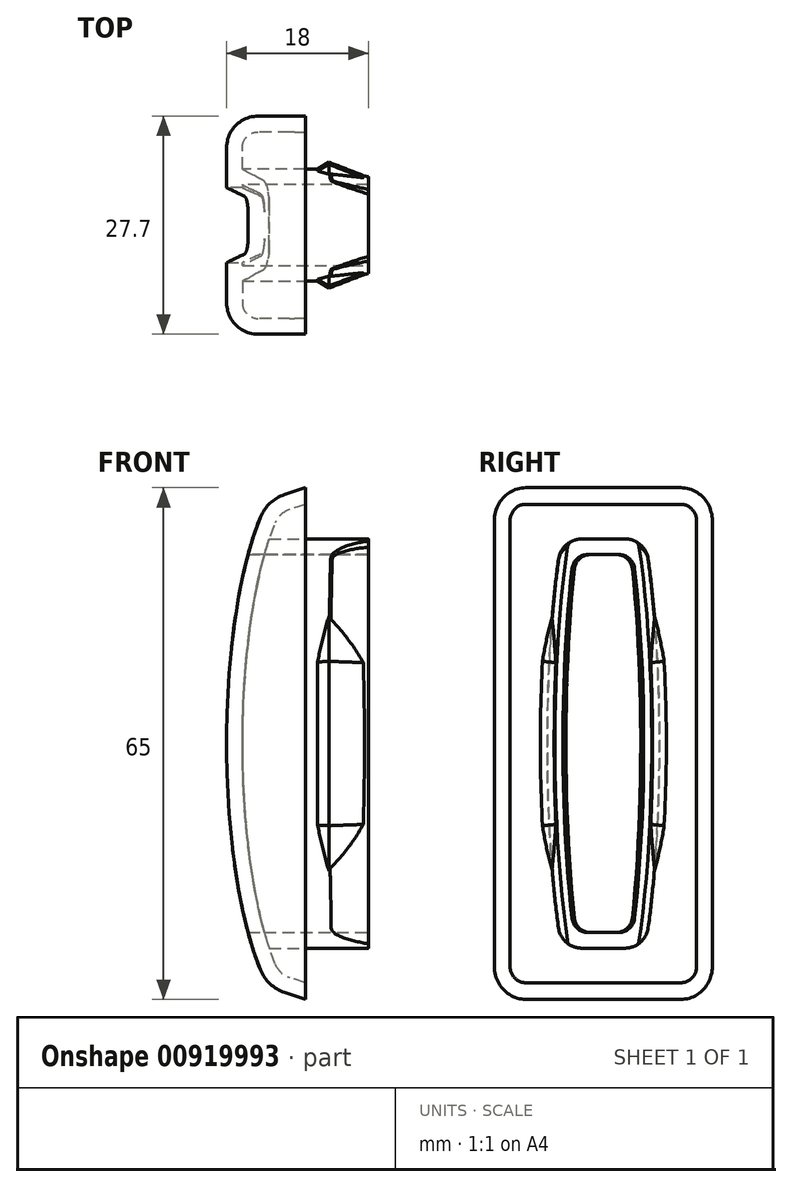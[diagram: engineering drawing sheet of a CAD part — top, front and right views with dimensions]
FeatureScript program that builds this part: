
annotation { "Feature Type Name" : "Feature", "Feature Type Description" : "" }
export const myFeature = defineFeature(function(context is Context, id is Id, definition is map)
    precondition{}
    {
        {
            var Q0;
            Q0=qCreatedBy(makeId("Front.planeOp"),FACE);
            var sketch = newSketch(context, id + "F0", { "sketchPlane" : qUnion([Q0])});
            skLineSegment(sketch, "E0", {"start": v(0, 32.5) * mm, "end": v(0, -32.5) * mm});
            skPoint(sketch, "E1", {"position": v(-10, 0) * mm});
            skPoint(sketch, "E2", {"position": v(0, 35) * mm});
            skEllipse(sketch, "E3", {"center": v(0, 0) * mm, "majorRadius": 35 * mm, "minorRadius": 10 * mm, "majorAxis": v(0, 1)});
            skPoint(sketch, "E4", {"position": v(-3, 31.5) * mm});
            skPoint(sketch, "E5", {"position": v(-3, -31.5) * mm});
            skLineSegment(sketch, "E6", {"start": v(0, -32.5) * mm, "end": v(-3, -31.5) * mm});
            skLineSegment(sketch, "E7", {"start": v(-3, -31.5) * mm, "end": v(-4.67, -30.94) * mm});
            skLineSegment(sketch, "E8", {"start": v(0, 32.5) * mm, "end": v(-3, 31.5) * mm});
            skLineSegment(sketch, "E9", {"start": v(-3, 31.5) * mm, "end": v(-4.67, 30.94) * mm});
            skSolve(sketch);
        }
        {
            var Q0;
            Q0=makeQuery(id+"F0.imprint","IMPRINT",FACE,{"disambiguationData":[TD([[makeQuery(id+"F0.imprint","IMPRINT",EDGE,{"derivedFrom":sQuery(id+"F0.wireOp",EDGE,"E0")}),-1.0]])]});
            extrude(context, id + "F1", {"entities" : qUnion([Q0]), "depth" : 13.85 * mm, "offsetDistance" : 25 * mm, "hasSecondDirection" : true, "secondDirectionOppositeDirection" : true, "secondDirectionDepth" : 13.85 * mm});
        }
        {
            var Q0;
            Q0=makeQuery(id+"F1.opExtrude","SWEPT_EDGE",EDGE,{"disambiguationData":[OSD([sQuery(id+"F0.wireOp",EDGE,"E3"),sQuery(id+"F0.wireOp",EDGE,"E7")])]});
            var Q1;
            Q1=makeQuery(id+"F1.opExtrude","SWEPT_EDGE",EDGE,{"disambiguationData":[OSD([sQuery(id+"F0.wireOp",EDGE,"E3"),sQuery(id+"F0.wireOp",EDGE,"E9")])]});
            fillet(context, id + "F2", {"entities" : qUnion([Q0, Q1]), "radius" : 5 * mm, "tangentPropagation" : true, "allowEdgeOverflow" : false});
        }
        {
            var Q0;
            Q0=makeQuery(id+"F1.opExtrude","CAP_EDGE",EDGE,{"disambiguationData":[OSD([sQuery(id+"F0.wireOp",EDGE,"E3")])],"isStart":false});
            var Q1;
            Q1=makeQuery(id+"F1.opExtrude","CAP_EDGE",EDGE,{"disambiguationData":[OSD([sQuery(id+"F0.wireOp",EDGE,"E3")])],"isStart":true});
            fillet(context, id + "F3", {"entities" : qUnion([Q0, Q1]), "radius" : 4 * mm, "tangentPropagation" : true, "allowEdgeOverflow" : false});
        }
        {
            var Q0;
            Q0=makeQuery(id+"F1.opExtrude","SWEPT_FACE",FACE,{"disambiguationData":[OSD([sQuery(id+"F0.wireOp",EDGE,"E0")])]});
            shell(context, id + "F4", {"entities" : qUnion([Q0]), "thickness" : 2 * mm});
        }
        {
            var Q0;
            Q0=qCreatedBy(makeId("Right.planeOp"),FACE);
            var sketch = newSketch(context, id + "F5", { "sketchPlane" : qUnion([Q0])});
            skPoint(sketch, "E10", {"position": v(0, 24) * mm});
            skPoint(sketch, "E11", {"position": v(5.12, 0) * mm});
            skPoint(sketch, "E12", {"position": v(3.5, 24.03) * mm});
            skPoint(sketch, "E13", {"position": v(0, 35) * mm});
            skEllipse(sketch, "E14", {"center": v(0, 0) * mm, "majorRadius": 5.12 * mm, "minorRadius": 35 * mm, "majorAxis": v(1, 0)});
            skLineSegment(sketch, "E15", {"start": v(0, 24) * mm, "end": v(7.2, 24.03) * mm});
            skLineSegment(sketch, "E16", {"start": v(0, -24) * mm, "end": v(3.73, -24) * mm});
            skLineSegment(sketch, "E17", {"start": v(0, -24) * mm, "end": v(-3.73, -24) * mm});
            skPoint(sketch, "E18", {"position": v(-4.75, 0) * mm});
            skEllipse(sketch, "E19", {"center": v(0, 0) * mm, "majorRadius": 4.75 * mm, "minorRadius": 35 * mm, "majorAxis": v(-1, 0)});
            skLineSegment(sketch, "E20", {"start": v(0, 24) * mm, "end": v(-5.9, 24) * mm});
            skLineSegment(sketch, "E21", {"start": v(-5.36, 25.98) * mm, "end": v(6.58, 26.03) * mm});
            skLineSegment(sketch, "E22", {"start": v(-8.21, -26) * mm, "end": v(8.3, -26) * mm});
            skPoint(sketch, "E23", {"position": v(7.12, 0) * mm});
            skPoint(sketch, "E24", {"position": v(0, 39) * mm});
            skEllipse(sketch, "E25", {"center": v(0, 0) * mm, "majorRadius": 7.12 * mm, "minorRadius": 39 * mm, "majorAxis": v(1, 0)});
            skPoint(sketch, "E26", {"position": v(6.12, 0) * mm});
            skPoint(sketch, "E27", {"position": v(0, 37) * mm});
            skEllipse(sketch, "E28", {"center": v(0, 0) * mm, "majorRadius": 6.12 * mm, "minorRadius": 37 * mm, "majorAxis": v(1, 0)});
            skSolve(sketch);
        }
        {
            var Q0;
            {var subQ5=sQuery(id+"F5.wireOp",EDGE,"E15");var subQ8=sQuery(id+"F5.wireOp",EDGE,"E20");var subQ9=makeQuery(id+"F5.imprint","INTERSECT",VERTEX,{"derivedFrom":[subQ5,subQ8]});Q0=makeQuery(id+"F5.imprint","IMPRINT",FACE,{"disambiguationData":[TD([[makeQuery(id+"F5.imprint","IMPRINT",EDGE,{"disambiguationData":[TD([[subQ9,-1.0]])],"derivedFrom":subQ5}),-1.0]])]});}
            extrude(context, id + "F6", {"entities" : qUnion([Q0]), "operationType" : NewBodyOperationType.REMOVE, "endBound" : BoundingType.THROUGH_ALL, "oppositeDirection" : true, "depth" : 25 * mm, "offsetDistance" : 25 * mm});
        }
        {
            var Q0;
            Q0=makeQuery(id+"F6.boolean.opBoolean","COPY",EDGE,{"derivedFrom":makeQuery(id+"F6.opExtrude","SWEPT_EDGE",EDGE,{"disambiguationData":[OSD([sQuery(id+"F5.wireOp",EDGE,"E19"),sQuery(id+"F5.wireOp",EDGE,"E20")])]})});
            var Q1;
            Q1=makeQuery(id+"F6.boolean.opBoolean","COPY",EDGE,{"derivedFrom":makeQuery(id+"F6.opExtrude","SWEPT_EDGE",EDGE,{"disambiguationData":[OSD([sQuery(id+"F5.wireOp",EDGE,"E15"),sQuery(id+"F5.wireOp",EDGE,"E19")])]})});
            var Q2;
            Q2=makeQuery(id+"F6.boolean.opBoolean","COPY",EDGE,{"derivedFrom":makeQuery(id+"F6.opExtrude","SWEPT_EDGE",EDGE,{"disambiguationData":[OSD([sQuery(id+"F5.wireOp",EDGE,"E16"),sQuery(id+"F5.wireOp",EDGE,"E19")])]})});
            var Q3;
            Q3=makeQuery(id+"F6.boolean.opBoolean","COPY",EDGE,{"derivedFrom":makeQuery(id+"F6.opExtrude","SWEPT_EDGE",EDGE,{"disambiguationData":[OSD([sQuery(id+"F5.wireOp",EDGE,"E17"),sQuery(id+"F5.wireOp",EDGE,"E19")])]})});
            fillet(context, id + "F7", {"entities" : qUnion([Q0, Q1, Q2, Q3]), "radius" : 2 * mm, "tangentPropagation" : true, "allowEdgeOverflow" : false});
        }
        {
            var Q0;
            {var subQ3=sQuery(id+"F5.wireOp",EDGE,"E14");var subQ5=makeQuery(id+"F5.imprint","INTERSECT",VERTEX,{"derivedFrom":[subQ3,sQuery(id+"F5.wireOp",EDGE,"E16")]});Q0=makeQuery(id+"F5.imprint","IMPRINT",FACE,{"disambiguationData":[TD([[makeQuery(id+"F5.imprint","IMPRINT",EDGE,{"disambiguationData":[TD([[subQ5,1.0]])],"derivedFrom":subQ3}),-1.0]])]});}
            var Q1;
            {var subQ3=sQuery(id+"F5.wireOp",EDGE,"E14");var subQ5=makeQuery(id+"F5.imprint","INTERSECT",VERTEX,{"derivedFrom":[subQ3,sQuery(id+"F5.wireOp",EDGE,"E17")]});Q1=makeQuery(id+"F5.imprint","IMPRINT",FACE,{"disambiguationData":[TD([[makeQuery(id+"F5.imprint","IMPRINT",EDGE,{"disambiguationData":[TD([[subQ5,1.0]])],"derivedFrom":subQ3}),-1.0]])]});}
            var Q2;
            {var subQ0=sQuery(id+"F5.wireOp",EDGE,"E15");var subQ1=sQuery(id+"F5.wireOp",EDGE,"E14");var subQ2=makeQuery(id+"F5.imprint","INTERSECT",VERTEX,{"derivedFrom":[subQ1,subQ0]});Q2=makeQuery(id+"F5.imprint","IMPRINT",FACE,{"disambiguationData":[TD([[makeQuery(id+"F5.imprint","IMPRINT",EDGE,{"disambiguationData":[TD([[subQ2,-1.0]])],"derivedFrom":subQ1}),-1.0]])]});}
            var Q3;
            {var subQ0=sQuery(id+"F5.wireOp",EDGE,"E15");var subQ1=sQuery(id+"F5.wireOp",EDGE,"E14");var subQ2=makeQuery(id+"F5.imprint","INTERSECT",VERTEX,{"derivedFrom":[subQ1,subQ0]});Q3=makeQuery(id+"F5.imprint","IMPRINT",FACE,{"disambiguationData":[TD([[makeQuery(id+"F5.imprint","IMPRINT",EDGE,{"disambiguationData":[TD([[subQ2,-1.0]])],"derivedFrom":subQ1}),1.0]])]});}
            var Q4;
            {var subQ0=sQuery(id+"F5.wireOp",EDGE,"E20");var subQ1=sQuery(id+"F5.wireOp",EDGE,"E15");var subQ2=makeQuery(id+"F5.imprint","INTERSECT",VERTEX,{"derivedFrom":[subQ1,subQ0]});Q4=makeQuery(id+"F5.imprint","IMPRINT",FACE,{"disambiguationData":[TD([[makeQuery(id+"F5.imprint","IMPRINT",EDGE,{"disambiguationData":[TD([[subQ2,-1.0]])],"derivedFrom":subQ1}),1.0]])]});}
            var Q5;
            {var subQ0=sQuery(id+"F5.wireOp",EDGE,"E21");var subQ1=sQuery(id+"F5.wireOp",EDGE,"E14");var subQ2=makeQuery(id+"F5.imprint","INTERSECT",VERTEX,{"disambiguationData":[OD(0.0)],"derivedFrom":[subQ1,subQ0]});Q5=makeQuery(id+"F5.imprint","IMPRINT",FACE,{"disambiguationData":[TD([[makeQuery(id+"F5.imprint","IMPRINT",EDGE,{"disambiguationData":[TD([[subQ2,-1.0]])],"derivedFrom":subQ1}),1.0]])]});}
            var Q6;
            {var subQ0=sQuery(id+"F5.wireOp",EDGE,"E21");var subQ1=sQuery(id+"F5.wireOp",EDGE,"E14");var subQ2=makeQuery(id+"F5.imprint","INTERSECT",VERTEX,{"disambiguationData":[OD(0.0)],"derivedFrom":[subQ1,subQ0]});Q6=makeQuery(id+"F5.imprint","IMPRINT",FACE,{"disambiguationData":[TD([[makeQuery(id+"F5.imprint","IMPRINT",EDGE,{"disambiguationData":[TD([[subQ2,-1.0]])],"derivedFrom":subQ1}),-1.0]])]});}
            var Q7;
            {var subQ0=sQuery(id+"F5.wireOp",EDGE,"E17");var subQ1=sQuery(id+"F5.wireOp",EDGE,"E14");var subQ2=makeQuery(id+"F5.imprint","INTERSECT",VERTEX,{"derivedFrom":[subQ1,subQ0]});Q7=makeQuery(id+"F5.imprint","IMPRINT",FACE,{"disambiguationData":[TD([[makeQuery(id+"F5.imprint","IMPRINT",EDGE,{"disambiguationData":[TD([[subQ2,-1.0]])],"derivedFrom":subQ1}),1.0]])]});}
            var Q8;
            {var subQ0=sQuery(id+"F5.wireOp",EDGE,"E16");var subQ1=sQuery(id+"F5.wireOp",EDGE,"E14");var subQ2=makeQuery(id+"F5.imprint","INTERSECT",VERTEX,{"derivedFrom":[subQ1,subQ0]});Q8=makeQuery(id+"F5.imprint","IMPRINT",FACE,{"disambiguationData":[TD([[makeQuery(id+"F5.imprint","IMPRINT",EDGE,{"disambiguationData":[TD([[subQ2,1.0]])],"derivedFrom":subQ1}),1.0]])]});}
            var Q9;
            {var subQ1=sQuery(id+"F5.wireOp",EDGE,"E17");var subQ5=sQuery(id+"F5.wireOp",EDGE,"E16");var subQ6=makeQuery(id+"F5.imprint","INTERSECT",VERTEX,{"derivedFrom":[subQ5,subQ1]});Q9=makeQuery(id+"F5.imprint","IMPRINT",FACE,{"disambiguationData":[TD([[makeQuery(id+"F5.imprint","IMPRINT",EDGE,{"disambiguationData":[TD([[subQ6,-1.0]])],"derivedFrom":subQ5}),-1.0]])]});}
            var Q10;
            {var subQ0=sQuery(id+"F5.wireOp",EDGE,"E25");var subQ1=sQuery(id+"F5.wireOp",EDGE,"E20");var subQ2=makeQuery(id+"F5.imprint","INTERSECT",VERTEX,{"derivedFrom":[subQ1,subQ0]});Q10=makeQuery(id+"F5.imprint","IMPRINT",FACE,{"disambiguationData":[TD([[makeQuery(id+"F5.imprint","IMPRINT",EDGE,{"disambiguationData":[TD([[subQ2,1.0]])],"derivedFrom":subQ1}),1.0]])]});}
            var Q11;
            {var subQ0=sQuery(id+"F5.wireOp",EDGE,"E25");var subQ1=sQuery(id+"F5.wireOp",EDGE,"E15");var subQ2=makeQuery(id+"F5.imprint","INTERSECT",VERTEX,{"derivedFrom":[subQ1,subQ0]});Q11=makeQuery(id+"F5.imprint","IMPRINT",FACE,{"disambiguationData":[TD([[makeQuery(id+"F5.imprint","IMPRINT",EDGE,{"disambiguationData":[TD([[subQ2,1.0]])],"derivedFrom":subQ1}),-1.0]])]});}
            var Q12;
            {var subQ0=sQuery(id+"F5.wireOp",EDGE,"E25");var subQ1=sQuery(id+"F5.wireOp",EDGE,"E20");var subQ2=makeQuery(id+"F5.imprint","INTERSECT",VERTEX,{"derivedFrom":[subQ1,subQ0]});Q12=makeQuery(id+"F5.imprint","IMPRINT",FACE,{"disambiguationData":[TD([[makeQuery(id+"F5.imprint","IMPRINT",EDGE,{"disambiguationData":[TD([[subQ2,1.0]])],"derivedFrom":subQ1}),-1.0]])]});}
            var Q13;
            {var subQ0=sQuery(id+"F5.wireOp",EDGE,"E25");var subQ1=sQuery(id+"F5.wireOp",EDGE,"E15");var subQ2=makeQuery(id+"F5.imprint","INTERSECT",VERTEX,{"derivedFrom":[subQ1,subQ0]});Q13=makeQuery(id+"F5.imprint","IMPRINT",FACE,{"disambiguationData":[TD([[makeQuery(id+"F5.imprint","IMPRINT",EDGE,{"disambiguationData":[TD([[subQ2,1.0]])],"derivedFrom":subQ1}),1.0]])]});}
            extrude(context, id + "F8", {"entities" : qUnion([Q0, Q1, Q2, Q3, Q4, Q5, Q6, Q7, Q8, Q9, Q10, Q11, Q12, Q13]), "operationType" : NewBodyOperationType.ADD, "endBound" : BoundingType.UP_TO_NEXT, "oppositeDirection" : true, "depth" : 25 * mm, "offsetDistance" : 25 * mm, "hasSecondDirection" : true, "secondDirectionOppositeDirection" : false, "secondDirectionDepth" : 3 * mm});
        }
        {
            var Q0;
            {var subQ1=sQuery(id+"F5.wireOp",EDGE,"E14");var subQ8=makeQuery(id+"F5.imprint","INTERSECT",VERTEX,{"derivedFrom":[subQ1,sQuery(id+"F5.wireOp",EDGE,"E16")]});Q0=makeQuery(id+"F5.imprint","IMPRINT",FACE,{"disambiguationData":[TD([[makeQuery(id+"F5.imprint","IMPRINT",EDGE,{"disambiguationData":[TD([[subQ8,1.0]])],"derivedFrom":subQ1}),-1.0]])]});}
            var Q1;
            {var subQ0=sQuery(id+"F5.wireOp",EDGE,"E16");var subQ1=sQuery(id+"F5.wireOp",EDGE,"E14");var subQ2=makeQuery(id+"F5.imprint","INTERSECT",VERTEX,{"derivedFrom":[subQ1,subQ0]});Q1=makeQuery(id+"F5.imprint","IMPRINT",FACE,{"disambiguationData":[TD([[makeQuery(id+"F5.imprint","IMPRINT",EDGE,{"disambiguationData":[TD([[subQ2,1.0]])],"derivedFrom":subQ1}),1.0]])]});}
            var Q2;
            {var subQ1=sQuery(id+"F5.wireOp",EDGE,"E17");var subQ5=sQuery(id+"F5.wireOp",EDGE,"E16");var subQ6=makeQuery(id+"F5.imprint","INTERSECT",VERTEX,{"derivedFrom":[subQ5,subQ1]});Q2=makeQuery(id+"F5.imprint","IMPRINT",FACE,{"disambiguationData":[TD([[makeQuery(id+"F5.imprint","IMPRINT",EDGE,{"disambiguationData":[TD([[subQ6,-1.0]])],"derivedFrom":subQ5}),-1.0]])]});}
            var Q3;
            {var subQ0=sQuery(id+"F5.wireOp",EDGE,"E17");var subQ1=sQuery(id+"F5.wireOp",EDGE,"E14");var subQ2=makeQuery(id+"F5.imprint","INTERSECT",VERTEX,{"derivedFrom":[subQ1,subQ0]});Q3=makeQuery(id+"F5.imprint","IMPRINT",FACE,{"disambiguationData":[TD([[makeQuery(id+"F5.imprint","IMPRINT",EDGE,{"disambiguationData":[TD([[subQ2,-1.0]])],"derivedFrom":subQ1}),1.0]])]});}
            var Q4;
            {var subQ1=sQuery(id+"F5.wireOp",EDGE,"E14");var subQ8=makeQuery(id+"F5.imprint","INTERSECT",VERTEX,{"derivedFrom":[subQ1,sQuery(id+"F5.wireOp",EDGE,"E17")]});Q4=makeQuery(id+"F5.imprint","IMPRINT",FACE,{"disambiguationData":[TD([[makeQuery(id+"F5.imprint","IMPRINT",EDGE,{"disambiguationData":[TD([[subQ8,1.0]])],"derivedFrom":subQ1}),-1.0]])]});}
            var Q5;
            {var subQ0=sQuery(id+"F5.wireOp",EDGE,"E15");var subQ1=sQuery(id+"F5.wireOp",EDGE,"E14");var subQ2=makeQuery(id+"F5.imprint","INTERSECT",VERTEX,{"derivedFrom":[subQ1,subQ0]});Q5=makeQuery(id+"F5.imprint","IMPRINT",FACE,{"disambiguationData":[TD([[makeQuery(id+"F5.imprint","IMPRINT",EDGE,{"disambiguationData":[TD([[subQ2,-1.0]])],"derivedFrom":subQ1}),-1.0]])]});}
            var Q6;
            {var subQ0=sQuery(id+"F5.wireOp",EDGE,"E15");var subQ1=sQuery(id+"F5.wireOp",EDGE,"E14");var subQ2=makeQuery(id+"F5.imprint","INTERSECT",VERTEX,{"derivedFrom":[subQ1,subQ0]});Q6=makeQuery(id+"F5.imprint","IMPRINT",FACE,{"disambiguationData":[TD([[makeQuery(id+"F5.imprint","IMPRINT",EDGE,{"disambiguationData":[TD([[subQ2,-1.0]])],"derivedFrom":subQ1}),1.0]])]});}
            var Q7;
            {var subQ0=sQuery(id+"F5.wireOp",EDGE,"E20");var subQ1=sQuery(id+"F5.wireOp",EDGE,"E15");var subQ2=makeQuery(id+"F5.imprint","INTERSECT",VERTEX,{"derivedFrom":[subQ1,subQ0]});Q7=makeQuery(id+"F5.imprint","IMPRINT",FACE,{"disambiguationData":[TD([[makeQuery(id+"F5.imprint","IMPRINT",EDGE,{"disambiguationData":[TD([[subQ2,-1.0]])],"derivedFrom":subQ1}),1.0]])]});}
            var Q8;
            {var subQ0=sQuery(id+"F5.wireOp",EDGE,"E21");var subQ1=sQuery(id+"F5.wireOp",EDGE,"E14");var subQ2=makeQuery(id+"F5.imprint","INTERSECT",VERTEX,{"disambiguationData":[OD(0.0)],"derivedFrom":[subQ1,subQ0]});Q8=makeQuery(id+"F5.imprint","IMPRINT",FACE,{"disambiguationData":[TD([[makeQuery(id+"F5.imprint","IMPRINT",EDGE,{"disambiguationData":[TD([[subQ2,-1.0]])],"derivedFrom":subQ1}),1.0]])]});}
            var Q9;
            {var subQ0=sQuery(id+"F5.wireOp",EDGE,"E21");var subQ1=sQuery(id+"F5.wireOp",EDGE,"E14");var subQ2=makeQuery(id+"F5.imprint","INTERSECT",VERTEX,{"disambiguationData":[OD(0.0)],"derivedFrom":[subQ1,subQ0]});Q9=makeQuery(id+"F5.imprint","IMPRINT",FACE,{"disambiguationData":[TD([[makeQuery(id+"F5.imprint","IMPRINT",EDGE,{"disambiguationData":[TD([[subQ2,-1.0]])],"derivedFrom":subQ1}),-1.0]])]});}
            extrude(context, id + "F9", {"entities" : qUnion([Q0, Q1, Q2, Q3, Q4, Q5, Q6, Q7, Q8, Q9]), "operationType" : NewBodyOperationType.ADD, "depth" : 8 * mm, "offsetDistance" : 25 * mm});
        }
        {
            var Q0;
            Q0=makeQuery(id+"F8.opExtrude","CAP_FACE",FACE,{"disambiguationData":[OSD([sQuery(id+"F5.wireOp",EDGE,"E14"),sQuery(id+"F5.wireOp",EDGE,"E15"),sQuery(id+"F5.wireOp",EDGE,"E16"),sQuery(id+"F5.wireOp",EDGE,"E17"),sQuery(id+"F5.wireOp",EDGE,"E20"),sQuery(id+"F5.wireOp",EDGE,"E21"),sQuery(id+"F5.wireOp",EDGE,"E22"),sQuery(id+"F5.wireOp",EDGE,"E25")])],"isStart":true});
            var Q1;
            Q1=makeQuery(id+"F9.opExtrude","CAP_FACE",FACE,{"disambiguationData":[OSD([sQuery(id+"F5.wireOp",EDGE,"E14"),sQuery(id+"F5.wireOp",EDGE,"E15"),sQuery(id+"F5.wireOp",EDGE,"E16"),sQuery(id+"F5.wireOp",EDGE,"E17"),sQuery(id+"F5.wireOp",EDGE,"E20"),sQuery(id+"F5.wireOp",EDGE,"E21"),sQuery(id+"F5.wireOp",EDGE,"E22"),sQuery(id+"F5.wireOp",EDGE,"E28")])],"isStart":false});
            var Q2;
            {var subQ0=sQuery(id+"F5.wireOp",EDGE,"E28");var subQ1=makeQuery(id+"F5.imprint","INTERSECT",VERTEX,{"derivedFrom":[sQuery(id+"F5.wireOp",EDGE,"E15"),subQ0]});Q2=makeQuery(id+"F9.opExtrude","CAP_EDGE",EDGE,{"disambiguationData":[OSD([subQ0]),TDD([makeQuery(id+"F5.imprint","IMPRINT",EDGE,{"disambiguationData":[TD([[subQ1,1.0]])],"derivedFrom":subQ0}),makeQuery(id+"F5.imprint","IMPRINT",EDGE,{"disambiguationData":[TD([[subQ1,-1.0]])],"derivedFrom":subQ0})])],"isStart":false});}
            var Q3;
            {var subQ0=sQuery(id+"F5.wireOp",EDGE,"E25");var subQ1=makeQuery(id+"F5.imprint","INTERSECT",VERTEX,{"derivedFrom":[sQuery(id+"F5.wireOp",EDGE,"E15"),subQ0]});Q3=makeQuery(id+"F8.opExtrude","CAP_EDGE",EDGE,{"disambiguationData":[OSD([subQ0]),TDD([makeQuery(id+"F5.imprint","IMPRINT",EDGE,{"disambiguationData":[TD([[subQ1,1.0]])],"derivedFrom":subQ0}),makeQuery(id+"F5.imprint","IMPRINT",EDGE,{"disambiguationData":[TD([[subQ1,-1.0]])],"derivedFrom":subQ0})])],"isStart":true});}
            loft(context, id + "F10", {"bodyType" : ToolBodyType.SURFACE, "sheetProfilesArray" : [{ "sheetProfileEntities" : qUnion([Q0]) }, { "sheetProfileEntities" : qUnion([Q1]) }], "wireProfilesArray" : [{ "wireProfileEntities" : qUnion([Q2]) }, { "wireProfileEntities" : qUnion([Q3]) }]});
        }
        {
            var Q0;
            {var subQ0=sQuery(id+"F5.wireOp",EDGE,"E25");var subQ1=makeQuery(id+"F5.imprint","INTERSECT",VERTEX,{"derivedFrom":[sQuery(id+"F5.wireOp",EDGE,"E20"),subQ0]});Q0=makeQuery(id+"F8.opExtrude","CAP_EDGE",EDGE,{"disambiguationData":[OSD([subQ0]),TDD([makeQuery(id+"F5.imprint","IMPRINT",EDGE,{"disambiguationData":[TD([[subQ1,1.0]])],"derivedFrom":subQ0}),makeQuery(id+"F5.imprint","IMPRINT",EDGE,{"disambiguationData":[TD([[subQ1,-1.0]])],"derivedFrom":subQ0})])],"isStart":true});}
            var Q1;
            {var subQ0=sQuery(id+"F5.wireOp",EDGE,"E28");var subQ1=makeQuery(id+"F5.imprint","INTERSECT",VERTEX,{"derivedFrom":[sQuery(id+"F5.wireOp",EDGE,"E20"),subQ0]});Q1=makeQuery(id+"F9.opExtrude","CAP_EDGE",EDGE,{"disambiguationData":[OSD([subQ0]),TDD([makeQuery(id+"F5.imprint","IMPRINT",EDGE,{"disambiguationData":[TD([[subQ1,1.0]])],"derivedFrom":subQ0}),makeQuery(id+"F5.imprint","IMPRINT",EDGE,{"disambiguationData":[TD([[subQ1,-1.0]])],"derivedFrom":subQ0})])],"isStart":false});}
            loft(context, id + "F11", {"bodyType" : ToolBodyType.SURFACE, "wireProfilesArray" : [{ "wireProfileEntities" : qUnion([Q0]) }, { "wireProfileEntities" : qUnion([Q1]) }]});
        }
        {
            var Q0;
            {var subQ0=sQuery(id+"F5.wireOp",EDGE,"E28");var subQ1=sQuery(id+"F5.wireOp",EDGE,"E15");var subQ2=makeQuery(id+"F5.imprint","INTERSECT",VERTEX,{"derivedFrom":[subQ1,subQ0]});var subQ3=sQuery(id+"F5.wireOp",EDGE,"E21");var subQ4=sQuery(id+"F5.wireOp",EDGE,"E22");Q0=makeQuery(id+"F9.boolean.opBoolean","INTERSECT",EDGE,{"derivedFrom":[makeQuery(id+"F8.opExtrude","CAP_FACE",FACE,{"disambiguationData":[OSD([sQuery(id+"F5.wireOp",EDGE,"E14"),subQ1,sQuery(id+"F5.wireOp",EDGE,"E16"),sQuery(id+"F5.wireOp",EDGE,"E17"),sQuery(id+"F5.wireOp",EDGE,"E20"),subQ3,subQ4,sQuery(id+"F5.wireOp",EDGE,"E25")])],"isStart":true}),makeQuery(id+"F9.opExtrude","SWEPT_FACE",FACE,{"disambiguationData":[OSD([subQ0]),TDD([makeQuery(id+"F5.imprint","IMPRINT",EDGE,{"disambiguationData":[TD([[subQ2,1.0]])],"derivedFrom":subQ0}),makeQuery(id+"F5.imprint","IMPRINT",EDGE,{"disambiguationData":[TD([[subQ2,-1.0]])],"derivedFrom":subQ0})])]})]});}
            chamfer(context, id + "F12", {"entities" : qUnion([Q0]), "chamferType" : ChamferType.OFFSET_ANGLE, "width" : 1 * mm, "oppositeDirection" : false, "angle" : 79 * degree});
        }
        {
            var Q0;
            {var subQ0=sQuery(id+"F5.wireOp",EDGE,"E28");var subQ1=sQuery(id+"F5.wireOp",EDGE,"E20");var subQ2=makeQuery(id+"F5.imprint","INTERSECT",VERTEX,{"derivedFrom":[subQ1,subQ0]});var subQ3=sQuery(id+"F5.wireOp",EDGE,"E22");var subQ4=sQuery(id+"F5.wireOp",EDGE,"E21");Q0=makeQuery(id+"F9.boolean.opBoolean","INTERSECT",EDGE,{"derivedFrom":[makeQuery(id+"F8.opExtrude","CAP_FACE",FACE,{"disambiguationData":[OSD([sQuery(id+"F5.wireOp",EDGE,"E14"),sQuery(id+"F5.wireOp",EDGE,"E15"),sQuery(id+"F5.wireOp",EDGE,"E16"),sQuery(id+"F5.wireOp",EDGE,"E17"),subQ1,subQ4,subQ3,sQuery(id+"F5.wireOp",EDGE,"E25")])],"isStart":true}),makeQuery(id+"F9.opExtrude","SWEPT_FACE",FACE,{"disambiguationData":[OSD([subQ0]),TDD([makeQuery(id+"F5.imprint","IMPRINT",EDGE,{"disambiguationData":[TD([[subQ2,1.0]])],"derivedFrom":subQ0}),makeQuery(id+"F5.imprint","IMPRINT",EDGE,{"disambiguationData":[TD([[subQ2,-1.0]])],"derivedFrom":subQ0})])]})]});}
            chamfer(context, id + "F13", {"entities" : qUnion([Q0]), "chamferType" : ChamferType.OFFSET_ANGLE, "width" : 1 * mm, "oppositeDirection" : false, "angle" : 79 * degree, "tangentPropagation" : true});
        }
        {
            var Q0;
            {var subQ0=sQuery(id+"F5.wireOp",EDGE,"E25");var subQ1=sQuery(id+"F5.wireOp",EDGE,"E22");Q0=makeQuery(id+"F8.opExtrude","SWEPT_EDGE",EDGE,{"disambiguationData":[OSD([subQ1,subQ0]),TDD([makeQuery(id+"F5.imprint","INTERSECT",VERTEX,{"disambiguationData":[OD(1.0)],"derivedFrom":[subQ1,subQ0]})])]});}
            var Q1;
            {var subQ0=sQuery(id+"F5.wireOp",EDGE,"E25");var subQ1=sQuery(id+"F5.wireOp",EDGE,"E22");Q1=makeQuery(id+"F8.opExtrude","SWEPT_EDGE",EDGE,{"disambiguationData":[OSD([subQ1,subQ0]),TDD([makeQuery(id+"F5.imprint","INTERSECT",VERTEX,{"disambiguationData":[OD(0.0)],"derivedFrom":[subQ1,subQ0]})])]});}
            var Q2;
            {var subQ0=sQuery(id+"F5.wireOp",EDGE,"E25");var subQ1=sQuery(id+"F5.wireOp",EDGE,"E21");Q2=makeQuery(id+"F8.opExtrude","SWEPT_EDGE",EDGE,{"disambiguationData":[OSD([subQ1,subQ0]),TDD([makeQuery(id+"F5.imprint","INTERSECT",VERTEX,{"disambiguationData":[OD(1.0)],"derivedFrom":[subQ1,subQ0]})])]});}
            var Q3;
            {var subQ0=sQuery(id+"F5.wireOp",EDGE,"E25");var subQ1=sQuery(id+"F5.wireOp",EDGE,"E21");Q3=makeQuery(id+"F8.opExtrude","SWEPT_EDGE",EDGE,{"disambiguationData":[OSD([subQ1,subQ0]),TDD([makeQuery(id+"F5.imprint","INTERSECT",VERTEX,{"disambiguationData":[OD(0.0)],"derivedFrom":[subQ1,subQ0]})])]});}
            fillet(context, id + "F14", {"entities" : qUnion([Q0, Q1, Q2, Q3]), "radius" : 3 * mm, "tangentPropagation" : true, "allowEdgeOverflow" : false});
        }
        {
            var Q0;
            Q0=qCreatedBy(makeId("Right.planeOp"),FACE);
            cPlane(context, id + "F15", {"entities" : qUnion([Q0]), "cplaneType" : CPlaneType.OFFSET, "offset" : 3 * mm, "width" : 150 * mm, "height" : 150 * mm});
        }
        {
            var Q0;
            Q0=qCreatedBy(id+"F15.planeOp",FACE);
            var sketch = newSketch(context, id + "F16", { "sketchPlane" : qUnion([Q0])});
            skPoint(sketch, "E29", {"position": v(-8, 0) * mm});
            skPoint(sketch, "E30", {"position": v(0, 40) * mm});
            skLineSegment(sketch, "E31", {"start": v(-7.46, 12) * mm, "end": v(7.46, 12) * mm});
            skLineSegment(sketch, "E32", {"start": v(-6.23, 17) * mm, "end": v(6.23, 17) * mm});
            skPoint(sketch, "E33", {"position": v(-8.5, 0) * mm});
            skPoint(sketch, "E34", {"position": v(0, 25) * mm});
            skEllipticalArc(sketch, "E35", {});
            skEllipticalArc(sketch, "E36.trimOffspring", {});
            skEllipticalArc(sketch, "E37.trimOffspring", {});
            skLineSegment(sketch, "E38", {"start": v(-6.23, -17) * mm, "end": v(6.23, -17) * mm});
            skEllipticalArc(sketch, "E39.trimOffspring", {});
            skEllipticalArc(sketch, "E40", {});
            skEllipticalArc(sketch, "E41.trimOffspring", {});
            const initialGuessF16  = {"E35": [0, 0, -1, 0, 0.0085, 0.025, 0.43108352761625657, 0.7477626346599209], "E36.trimOffspring": [0, 0, -1, 0, 0.008, 0.04, 6.018961952784559, 0.26422335439502653], "E37.trimOffspring": [0, 0, -1, 0, 0.0085, 0.025, 5.535422672519665, 5.852101779563329], "E39.trimOffspring": [0, 0, -1, 0, 0.0085, 0.025, 2.3938300189298722, 2.7105091259735365], "E40": [0, 0, -1, 0, 0.008, 0.04, 2.8773692991947666, 3.4058160079848196], "E41.trimOffspring": [0, 0, -1, 0, 0.0085, 0.025, 3.5726761812060497, 3.889355288249714], "E36.trimOffspring": [0, 0, -1, 0, 0.008, 0.04, 6.018961952784559, 0.26422335439502653]};
            skSetInitialGuess(sketch, initialGuessF16);
            skSolve(sketch);
        }
        {
            var Q0;
            Q0=qCreatedBy(makeId("Top.planeOp"),FACE);
            var sketch = newSketch(context, id + "F17", { "sketchPlane" : qUnion([Q0])});
            skPoint(sketch, "E42", {"position": v(3, -8) * mm});
            skPoint(sketch, "E43", {"position": v(3, 8) * mm});
            skPoint(sketch, "E44", {"position": v(1.5, -7.1) * mm});
            skPoint(sketch, "E45", {"position": v(7.9, -6.1) * mm});
            skLineSegment(sketch, "E46", {"start": v(1.5, -7.1) * mm, "end": v(3, -8) * mm});
            skLineSegment(sketch, "E47", {"start": v(7.9, -6.1) * mm, "end": v(3, -8) * mm});
            skLineSegment(sketch, "E48", {"start": v(1.5, -7.1) * mm, "end": v(7.9, -6.1) * mm});
            skLineSegment(sketch, "E49", {"start": v(10.3, 0) * mm, "end": v(1.68, 0) * mm});
            skLineSegment(sketch, "E50.MirrorCS", {"start": v(7.9, 6.1) * mm, "end": v(3, 8) * mm});
            skLineSegment(sketch, "E51.MirrorCS", {"start": v(1.5, 7.1) * mm, "end": v(3, 8) * mm});
            skLineSegment(sketch, "E52.MirrorCS", {"start": v(1.5, 7.1) * mm, "end": v(7.9, 6.1) * mm});
            skSolve(sketch);
        }
        {
            var Q0;
            Q0=makeQuery(id+"F17.imprint","IMPRINT",FACE,{"disambiguationData":[TD([[makeQuery(id+"F17.imprint","IMPRINT",EDGE,{"derivedFrom":sQuery(id+"F17.wireOp",EDGE,"E50.MirrorCS")}),1.0]])]});
            var Q1;
            Q1=sQuery(id+"F16.wireOp",EDGE,"E40");
            var Q2;
            Q2=sQuery(id+"F16.wireOp",EDGE,"E39.trimOffspring");
            var Q3;
            Q3=sQuery(id+"F16.wireOp",EDGE,"E41.trimOffspring");
            sweep(context, id + "F18", {"operationType" : NewBodyOperationType.ADD, "profiles" : qUnion([Q0]), "path" : qUnion([Q1, Q2, Q3])});
        }
        {
            var Q0;
            Q0=makeQuery(id+"F17.imprint","IMPRINT",FACE,{"disambiguationData":[TD([[makeQuery(id+"F17.imprint","IMPRINT",EDGE,{"derivedFrom":sQuery(id+"F17.wireOp",EDGE,"E46")}),1.0]])]});
            var Q1;
            Q1=sQuery(id+"F16.wireOp",EDGE,"E36.trimOffspring");
            var Q2;
            Q2=sQuery(id+"F16.wireOp",EDGE,"E37.trimOffspring");
            var Q3;
            Q3=sQuery(id+"F16.wireOp",EDGE,"E35");
            sweep(context, id + "F19", {"operationType" : NewBodyOperationType.ADD, "profiles" : qUnion([Q0]), "path" : qUnion([Q1, Q2, Q3])});
        }
        {
            var Q0;
            {var subQ0=sQuery(id+"F5.wireOp",EDGE,"E16");var subQ1=sQuery(id+"F5.wireOp",EDGE,"E14");var subQ2=makeQuery(id+"F5.imprint","INTERSECT",VERTEX,{"derivedFrom":[subQ1,subQ0]});Q0=makeQuery(id+"F5.imprint","IMPRINT",FACE,{"disambiguationData":[TD([[makeQuery(id+"F5.imprint","IMPRINT",EDGE,{"disambiguationData":[TD([[subQ2,-1.0]])],"derivedFrom":subQ1}),1.0]])]});}
            var Q1;
            {var subQ0=sQuery(id+"F5.wireOp",EDGE,"E17");var subQ1=sQuery(id+"F5.wireOp",EDGE,"E14");var subQ2=makeQuery(id+"F5.imprint","INTERSECT",VERTEX,{"derivedFrom":[subQ1,subQ0]});Q1=makeQuery(id+"F5.imprint","IMPRINT",FACE,{"disambiguationData":[TD([[makeQuery(id+"F5.imprint","IMPRINT",EDGE,{"disambiguationData":[TD([[subQ2,1.0]])],"derivedFrom":subQ1}),1.0]])]});}
            extrude(context, id + "F20", {"entities" : qUnion([Q0, Q1]), "operationType" : NewBodyOperationType.REMOVE, "depth" : 25 * mm, "offsetDistance" : 25 * mm});
        }
        {
            var Q0;
            {var subQ0=sQuery(id+"F5.wireOp",EDGE,"E15");var subQ1=sQuery(id+"F5.wireOp",EDGE,"E14");Q0=makeQuery(id+"F9.boolean.opBoolean","MERGE",EDGE,{"derivedFrom":[makeQuery(id+"F8.opExtrude","SWEPT_EDGE",EDGE,{"disambiguationData":[OSD([subQ1,subQ0])]}),makeQuery(id+"F9.opExtrude","SWEPT_EDGE",EDGE,{"disambiguationData":[OSD([subQ1,subQ0])]})]});}
            var Q1;
            {var subQ0=sQuery(id+"F5.wireOp",EDGE,"E20");var subQ1=sQuery(id+"F5.wireOp",EDGE,"E14");Q1=makeQuery(id+"F9.boolean.opBoolean","MERGE",EDGE,{"derivedFrom":[makeQuery(id+"F8.opExtrude","SWEPT_EDGE",EDGE,{"disambiguationData":[OSD([subQ1,subQ0])]}),makeQuery(id+"F9.opExtrude","SWEPT_EDGE",EDGE,{"disambiguationData":[OSD([subQ1,subQ0])]})]});}
            var Q2;
            {var subQ0=sQuery(id+"F5.wireOp",EDGE,"E17");var subQ1=sQuery(id+"F5.wireOp",EDGE,"E14");Q2=makeQuery(id+"F9.boolean.opBoolean","MERGE",EDGE,{"derivedFrom":[makeQuery(id+"F8.opExtrude","SWEPT_EDGE",EDGE,{"disambiguationData":[OSD([subQ1,subQ0])]}),makeQuery(id+"F9.opExtrude","SWEPT_EDGE",EDGE,{"disambiguationData":[OSD([subQ1,subQ0])]})]});}
            var Q3;
            {var subQ0=sQuery(id+"F5.wireOp",EDGE,"E16");var subQ1=sQuery(id+"F5.wireOp",EDGE,"E14");Q3=makeQuery(id+"F9.boolean.opBoolean","MERGE",EDGE,{"derivedFrom":[makeQuery(id+"F8.opExtrude","SWEPT_EDGE",EDGE,{"disambiguationData":[OSD([subQ1,subQ0])]}),makeQuery(id+"F9.opExtrude","SWEPT_EDGE",EDGE,{"disambiguationData":[OSD([subQ1,subQ0])]})]});}
            fillet(context, id + "F21", {"entities" : qUnion([Q0, Q1, Q2, Q3]), "radius" : 2 * mm, "tangentPropagation" : true, "allowEdgeOverflow" : false});
        }
        {
            var Q0;
            {var subQ0=sQuery(id+"F5.wireOp",EDGE,"E25");var subQ1=sQuery(id+"F5.wireOp",EDGE,"E21");Q0=makeQuery(id+"F14.opFillet","BLEND_EDGE",EDGE,{"blendedFrom":[makeQuery(id+"F8.opExtrude","SWEPT_EDGE",EDGE,{"disambiguationData":[OSD([subQ1,subQ0]),TDD([makeQuery(id+"F5.imprint","INTERSECT",VERTEX,{"disambiguationData":[OD(0.0)],"derivedFrom":[subQ1,subQ0]})])]}),makeQuery(id+"F13.opChamfer","BLEND_FACE",FACE,{"disambiguationData":[OSD([sQuery(id+"F5.wireOp",EDGE,"E14"),sQuery(id+"F5.wireOp",EDGE,"E15"),sQuery(id+"F5.wireOp",EDGE,"E16"),sQuery(id+"F5.wireOp",EDGE,"E17"),sQuery(id+"F5.wireOp",EDGE,"E20"),subQ1,sQuery(id+"F5.wireOp",EDGE,"E22"),subQ0,sQuery(id+"F5.wireOp",EDGE,"E28")])]})],"blendedInto":[makeQuery(id+"F13.opChamfer","BLEND_FACE",FACE,{"disambiguationData":[OSD([sQuery(id+"F5.wireOp",EDGE,"E14"),sQuery(id+"F5.wireOp",EDGE,"E15"),sQuery(id+"F5.wireOp",EDGE,"E16"),sQuery(id+"F5.wireOp",EDGE,"E17"),sQuery(id+"F5.wireOp",EDGE,"E20"),subQ1,sQuery(id+"F5.wireOp",EDGE,"E22"),subQ0,sQuery(id+"F5.wireOp",EDGE,"E28")])]})]});}
            var Q1;
            {var subQ0=sQuery(id+"F5.wireOp",EDGE,"E25");var subQ1=sQuery(id+"F5.wireOp",EDGE,"E21");Q1=makeQuery(id+"F14.opFillet","BLEND_EDGE",EDGE,{"blendedFrom":[makeQuery(id+"F8.opExtrude","SWEPT_EDGE",EDGE,{"disambiguationData":[OSD([subQ1,subQ0]),TDD([makeQuery(id+"F5.imprint","INTERSECT",VERTEX,{"disambiguationData":[OD(1.0)],"derivedFrom":[subQ1,subQ0]})])]}),makeQuery(id+"F12.opChamfer","BLEND_FACE",FACE,{"disambiguationData":[OSD([sQuery(id+"F5.wireOp",EDGE,"E14"),sQuery(id+"F5.wireOp",EDGE,"E15"),sQuery(id+"F5.wireOp",EDGE,"E16"),sQuery(id+"F5.wireOp",EDGE,"E17"),sQuery(id+"F5.wireOp",EDGE,"E20"),subQ1,sQuery(id+"F5.wireOp",EDGE,"E22"),subQ0,sQuery(id+"F5.wireOp",EDGE,"E28")])]})],"blendedInto":[makeQuery(id+"F12.opChamfer","BLEND_FACE",FACE,{"disambiguationData":[OSD([sQuery(id+"F5.wireOp",EDGE,"E14"),sQuery(id+"F5.wireOp",EDGE,"E15"),sQuery(id+"F5.wireOp",EDGE,"E16"),sQuery(id+"F5.wireOp",EDGE,"E17"),sQuery(id+"F5.wireOp",EDGE,"E20"),subQ1,sQuery(id+"F5.wireOp",EDGE,"E22"),subQ0,sQuery(id+"F5.wireOp",EDGE,"E28")])]})]});}
            var Q2;
            {var subQ0=sQuery(id+"F5.wireOp",EDGE,"E25");var subQ1=sQuery(id+"F5.wireOp",EDGE,"E22");Q2=makeQuery(id+"F14.opFillet","BLEND_EDGE",EDGE,{"blendedFrom":[makeQuery(id+"F8.opExtrude","SWEPT_EDGE",EDGE,{"disambiguationData":[OSD([subQ1,subQ0]),TDD([makeQuery(id+"F5.imprint","INTERSECT",VERTEX,{"disambiguationData":[OD(0.0)],"derivedFrom":[subQ1,subQ0]})])]}),makeQuery(id+"F13.opChamfer","BLEND_FACE",FACE,{"disambiguationData":[OSD([sQuery(id+"F5.wireOp",EDGE,"E14"),sQuery(id+"F5.wireOp",EDGE,"E15"),sQuery(id+"F5.wireOp",EDGE,"E16"),sQuery(id+"F5.wireOp",EDGE,"E17"),sQuery(id+"F5.wireOp",EDGE,"E20"),sQuery(id+"F5.wireOp",EDGE,"E21"),subQ1,subQ0,sQuery(id+"F5.wireOp",EDGE,"E28")])]})],"blendedInto":[makeQuery(id+"F13.opChamfer","BLEND_FACE",FACE,{"disambiguationData":[OSD([sQuery(id+"F5.wireOp",EDGE,"E14"),sQuery(id+"F5.wireOp",EDGE,"E15"),sQuery(id+"F5.wireOp",EDGE,"E16"),sQuery(id+"F5.wireOp",EDGE,"E17"),sQuery(id+"F5.wireOp",EDGE,"E20"),sQuery(id+"F5.wireOp",EDGE,"E21"),subQ1,subQ0,sQuery(id+"F5.wireOp",EDGE,"E28")])]})]});}
            var Q3;
            {var subQ0=sQuery(id+"F5.wireOp",EDGE,"E25");var subQ1=sQuery(id+"F5.wireOp",EDGE,"E22");Q3=makeQuery(id+"F14.opFillet","BLEND_EDGE",EDGE,{"blendedFrom":[makeQuery(id+"F8.opExtrude","SWEPT_EDGE",EDGE,{"disambiguationData":[OSD([subQ1,subQ0]),TDD([makeQuery(id+"F5.imprint","INTERSECT",VERTEX,{"disambiguationData":[OD(1.0)],"derivedFrom":[subQ1,subQ0]})])]}),makeQuery(id+"F12.opChamfer","BLEND_FACE",FACE,{"disambiguationData":[OSD([sQuery(id+"F5.wireOp",EDGE,"E14"),sQuery(id+"F5.wireOp",EDGE,"E15"),sQuery(id+"F5.wireOp",EDGE,"E16"),sQuery(id+"F5.wireOp",EDGE,"E17"),sQuery(id+"F5.wireOp",EDGE,"E20"),sQuery(id+"F5.wireOp",EDGE,"E21"),subQ1,subQ0,sQuery(id+"F5.wireOp",EDGE,"E28")])]})],"blendedInto":[makeQuery(id+"F12.opChamfer","BLEND_FACE",FACE,{"disambiguationData":[OSD([sQuery(id+"F5.wireOp",EDGE,"E14"),sQuery(id+"F5.wireOp",EDGE,"E15"),sQuery(id+"F5.wireOp",EDGE,"E16"),sQuery(id+"F5.wireOp",EDGE,"E17"),sQuery(id+"F5.wireOp",EDGE,"E20"),sQuery(id+"F5.wireOp",EDGE,"E21"),subQ1,subQ0,sQuery(id+"F5.wireOp",EDGE,"E28")])]})]});}
            fillet(context, id + "F22", {"entities" : qUnion([Q0, Q1, Q2, Q3]), "radius" : 1 * mm, "tangentPropagation" : true, "allowEdgeOverflow" : false});
        }
    });
